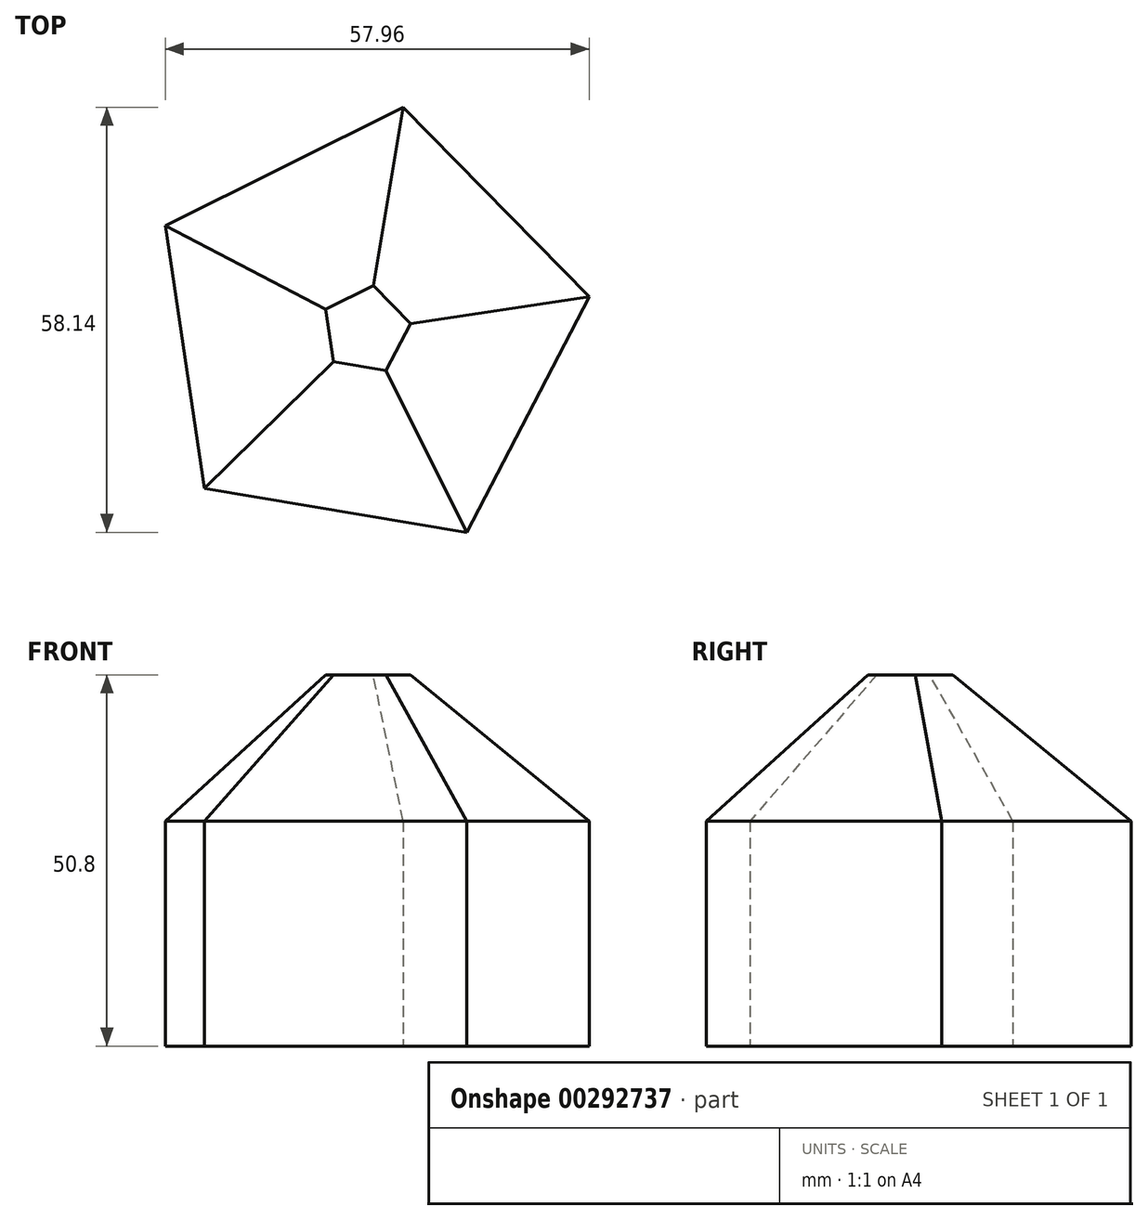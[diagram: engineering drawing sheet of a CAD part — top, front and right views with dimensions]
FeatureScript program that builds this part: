
annotation { "Feature Type Name" : "Feature", "Feature Type Description" : "" }
export const myFeature = defineFeature(function(context is Context, id is Id, definition is map)
    precondition{}
    {
        {
            var Q0;
            Q0=qCreatedBy(makeId("Top.planeOp"),FACE);
            var sketch = newSketch(context, id + "F0", { "sketchPlane" : qUnion([Q0])});
            skCircle(sketch, "E0.cCircle", {"center": v(0, 0) * mm, "radius": 25 * mm, "construction": true});
            skLineSegment(sketch, "E0.0", {"start": v(30.56, 4.55) * mm, "end": v(13.77, -27.66) * mm});
            skLineSegment(sketch, "E0.1", {"start": v(13.77, -27.66) * mm, "end": v(-22.05, -21.65) * mm});
            skLineSegment(sketch, "E0.2", {"start": v(-22.05, -21.65) * mm, "end": v(-27.4, 14.28) * mm});
            skLineSegment(sketch, "E0.3", {"start": v(-27.4, 14.28) * mm, "end": v(5.12, 30.48) * mm});
            skLineSegment(sketch, "E0.4", {"start": v(5.12, 30.48) * mm, "end": v(30.56, 4.55) * mm});
            skPoint(sketch, "E0.0.midPoint", {"position": v(22.17, -11.55) * mm});
            skSolve(sketch);
        }
        {
            var Q0;
            Q0=makeQuery(id+"F0.imprint","IMPRINT",FACE,{"disambiguationData":[TD([[makeQuery(id+"F0.imprint","IMPRINT",EDGE,{"derivedFrom":sQuery(id+"F0.wireOp",EDGE,"E0.0")}),-1.0]])]});
            extrude(context, id + "F1", {"entities" : qUnion([Q0]), "depth" : 50.8 * mm});
        }
        {
            var Q0;
            Q0=makeQuery(id+"F1.opExtrude","CAP_FACE",FACE,{"disambiguationData":[OSD([sQuery(id+"F0.wireOp",EDGE,"E0.0"),sQuery(id+"F0.wireOp",EDGE,"E0.1"),sQuery(id+"F0.wireOp",EDGE,"E0.2"),sQuery(id+"F0.wireOp",EDGE,"E0.3"),sQuery(id+"F0.wireOp",EDGE,"E0.4")])],"isStart":false});
            chamfer(context, id + "F2", {"entities" : qUnion([Q0]), "width" : 20 * mm, "tangentPropagation" : true});
        }
    });
